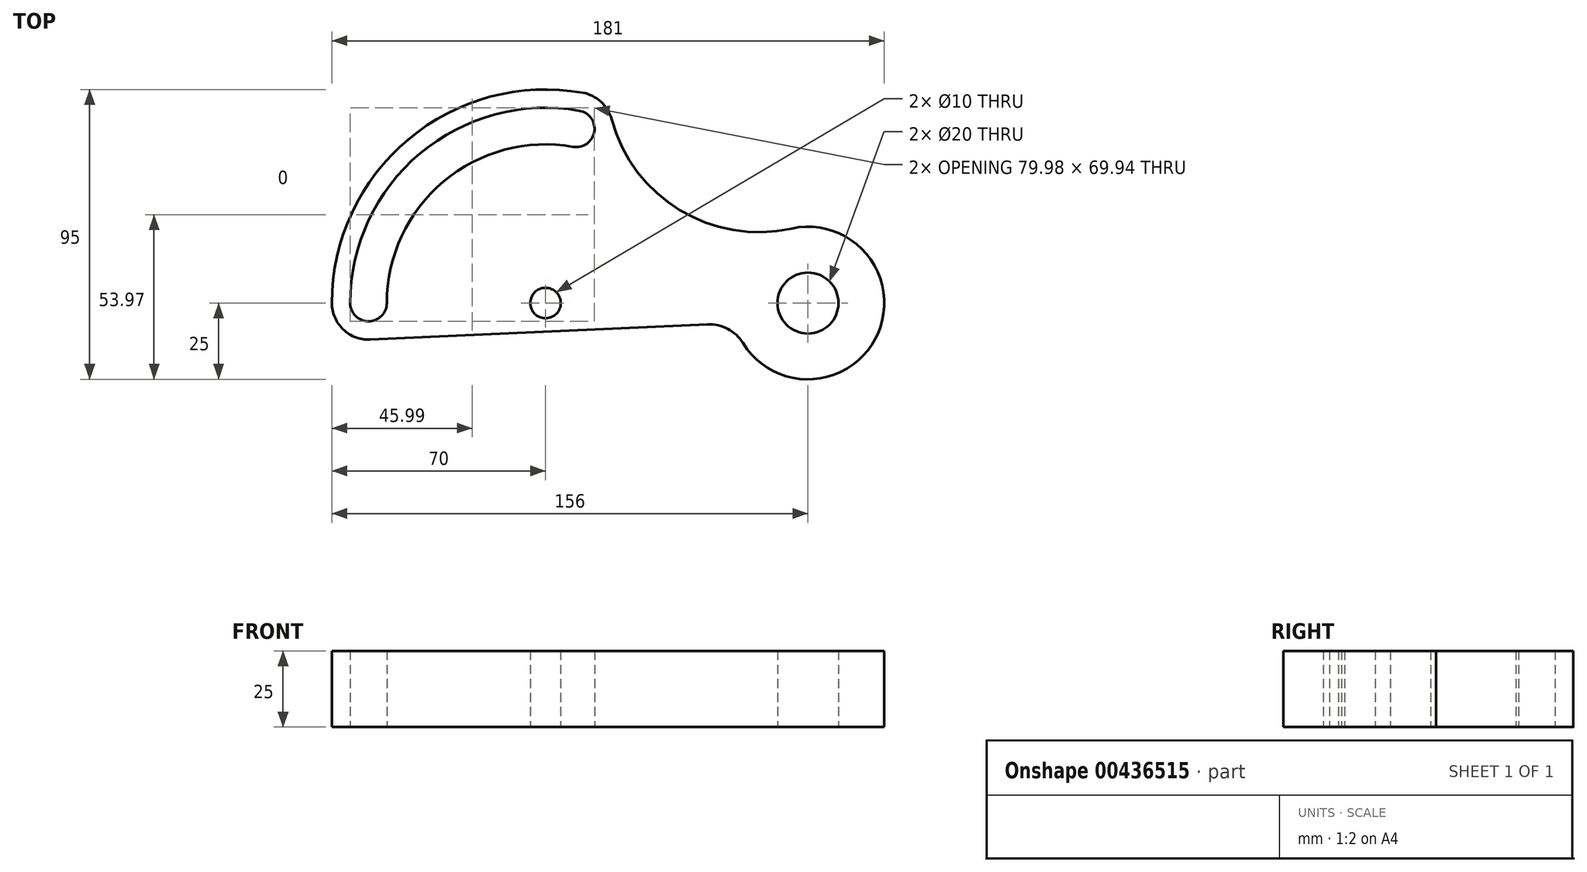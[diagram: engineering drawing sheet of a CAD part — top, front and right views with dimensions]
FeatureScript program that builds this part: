
annotation { "Feature Type Name" : "Feature", "Feature Type Description" : "" }
export const myFeature = defineFeature(function(context is Context, id is Id, definition is map)
    precondition{}
    {
        {
            var Q0;
            Q0=qCreatedBy(makeId("Top.planeOp"),FACE);
            var sketch = newSketch(context, id + "F0", { "sketchPlane" : qUnion([Q0])});
            skCircle(sketch, "E0", {"center": v(0, 0) * mm, "radius": 5 * mm});
            skCircle(sketch, "E1", {"center": v(86, 0) * mm, "radius": 10 * mm});
            skLineSegment(sketch, "E2", {"start": v(-77.57, 0) * mm, "end": v(86, 0) * mm, "construction": true});
            skLineSegment(sketch, "E3", {"start": v(0, 0) * mm, "end": v(12.3, 69.8) * mm, "construction": true});
            skArc(sketch, "E4", {"start": v(64.74, -13.16) * mm, "mid": v(109.02, -9.74) * mm, "end": v(80.64, 24.42) * mm});
            skArc(sketch, "E5", {"start": v(-53.66, -22.01) * mm, "mid": v(-40.64, 41.38) * mm, "end": v(22.97, 53.26) * mm, "construction": true});
            skArc(sketch, "E6", {"start": v(11.11, 63.03) * mm, "mid": v(15.98, 56.08) * mm, "end": v(9.03, 51.21) * mm});
            skArc(sketch, "E7", {"start": v(-64, 0) * mm, "mid": v(-58, -6) * mm, "end": v(-52, 0) * mm});
            skArc(sketch, "E8", {"start": v(12.16, 68.94) * mm, "mid": v(18.17, 65.97) * mm, "end": v(21.66, 60.24) * mm});
            skArc(sketch, "E9", {"start": v(-64, 0) * mm, "mid": v(-41.14, 49.03) * mm, "end": v(11.11, 63.03) * mm});
            skArc(sketch, "E10", {"start": v(-52, 0) * mm, "mid": v(-33.42, 39.83) * mm, "end": v(9.03, 51.21) * mm});
            skArc(sketch, "E11", {"start": v(-70, 0) * mm, "mid": v(-66.3, -8.67) * mm, "end": v(-57.46, -11.99) * mm});
            skArc(sketch, "E12", {"start": v(-70, 0) * mm, "mid": v(-45, 53.62) * mm, "end": v(12.16, 68.94) * mm});
            skArc(sketch, "E13", {"start": v(64.74, -13.16) * mm, "mid": v(59.76, -8.5) * mm, "end": v(53.1, -7.01) * mm});
            skLineSegment(sketch, "E14", {"start": v(-57.46, -11.99) * mm, "end": v(53.1, -7.01) * mm});
            skArc(sketch, "E15", {"start": v(21.66, 60.24) * mm, "mid": v(43.98, 30.52) * mm, "end": v(80.64, 24.42) * mm});
            skSolve(sketch);
        }
        {
            var Q0;
            Q0=makeQuery(id+"F0.imprint","IMPRINT",FACE,{"disambiguationData":[TD([[makeQuery(id+"F0.imprint","IMPRINT",EDGE,{"derivedFrom":sQuery(id+"F0.wireOp",EDGE,"E0")}),-1.0]])]});
            extrude(context, id + "F1", {"entities" : qUnion([Q0]), "depth" : 25 * mm});
        }
    });
